# Revit family: IS_IdealrainDual_Multiproduct_BIM_GB_A5834_A5862
name_source: partatom
category: Plumbing Fixtures
revit_build: Autodesk Revit MEP 2014 (Build: 20130308_1515(x64)
units: mm (PartAtom-declared; Revit-internal decimal feet)

## types (2) — shared parameters
Accessories = www.idealspec.co.uk
AreaUnits = millimeters
Assembly Code = C1030200
AssetType = Fixed
BREEAMApproved = No
Brand = Ideal Standard
Color = Chrome
ConnectionType = Plumbing
Default Elevation = 800 mm  [stored 2.62467 ft]
DurationUnit = year
ECA = No
ExpectedLife = 30
FaucetFunction = MIXED
FaucetOperation = LEVERHANDLE
Finish = Chrome
FlowRate = 16L/min @ 3bar
Help = www.idealspec.co.uk/contact-us.html
IfcExportAs = IfcValveType
IfcExportType = SHOWERS
InstallationInstructions = www.idealspec.co.uk/resources.html
LinearUnits = millimeters
ManufacturerURL = www.idealspec.co.uk
Material = Brass
MetalMtl = ISI_IdealStandard_Brassware_Chrome_Render
NBSDescription = Shower Fittings Package
NBSReference = 45-35-70/330
Name = ShowerMixers_IdealRain_A5691AA_IdealStandard
NominalLength = 1051 mm
NominalWidth = 200 mm
RubberMtl = ISI_IdealsStandard_Brassware_Rubber_Render
Shape = Sculptured
Size = 0 x 1051 x 200 mm
Space = Internal
SpareParts = www.fastpart-spares.co.uk
TMV3 = Yes
TestPressure = 10 Bar
URL = www.idealspec.co.uk
Uniclass2015Code = Pr_40_20_87_75
Uniclass2015Title = Shower Fittings Package
Uniclass2015Version = Product v1.1
Version = 1
VolumeUnits = Litres
WRAS = Yes
WarrantyDescription = Manufacturers Warranty
WarrantyDurationParts = 5
WarrantyDurationUnit = year
WaterEfficientProduct = No
WorkingPressure = 3 Bar
zero-valued in all types: CWFU, Cost, HWFU, NominalHeight, WFU

## per-type parameters (varying)
| type | BIMObjectName | BarCode | Description | ExposedSystem | Features | Model | NettWeight | ProductInformation | System | TapDepth |
| A5834AA - Idealrain Dual Shower System - M1 RainShower fixer Riser - M3 Handsprayer & Diverter | ISI_IdealStandard_ShowerMixers_IdealRain_A5834AA | 4015413327749 | Idealrain Dual shower system built-in, with M1 Rainshower, fixed riser, M3 handspray and diverter | No | Dual shower system built-in, with M1 Rainshower, fixed riser, M3 handspray and diverter | A5834AA | 5.3Kg | www.idealspec.co.uk/assets/datasheet/A5834AA | Yes | 122 mm  [stored 0.400262 ft] |
| A5862AA - Idealrain Dula Shower System Exposed - M1 RainShower fixer Riser - M3 Handsprayer & Diverter | ISI_IdealStandard_ShowerMixers_IdealRain_A5862AA | 4015413327763 | Idealrain Dual shower system exposed, with M1 Rainshower, fixed riser, M3 handspray and diverter | Yes | Dual shower system exposed, with M1 Rainshower, fixed riser, M3 handspray and diverter | A5862AA | 5.4Kg | www.idealspec.co.uk/assets/datasheet/A5862AA | No | 112 mm  [stored 0.367454 ft] |

note: [stored X ft] marks values corroborated as IEEE doubles in the binary element streams (Revit-internal decimal feet)

## geometry (parser evidence)
native form markers: Sweep x3
no freeform markers — native parametric forms only
